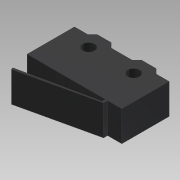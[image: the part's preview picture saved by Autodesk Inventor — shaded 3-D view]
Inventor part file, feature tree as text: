
AUTODESK INVENTOR PART (.ipt)
format: ipt  version: 2014 (Build 180170000, 170)  size: 117,760 bytes
history: native  units: mm
features: extrude x2, sketch x2, reference x1
ambient origin geometry x8: Origin, YZ Plane, XZ Plane, XY Plane, X Axis, Y Axis, Z Axis, Center Point
bodies: Solid1 (feature_tree)
feature tree (5):
  extrude  "Extrusion1"  Depth=9.0mm
  extrude  "Extrusion2"  TaperAngle=45.0deg  [1 undecoded]
  sketch  "Sketch1"  dims[d0=9.0mm d1=2.0mm]
  reference  "Reference1"
  sketch  "Sketch2"  dims[d2=1.0mm d3=45.0deg d4=45.0deg d5=45.0deg d6=3.0mm d7=3.0mm d8=1.5mm d9=2.5mm d10=2.5mm d11=1.5mm d12=6.4mm d13=0.0mm d14=6.4mm d15=0.0mm]
note: 1 required parameter value undecoded (feature->parameter linkage not recoverable at this tier; creation-order binding heuristic only, values carry confidence <= 0.55)
